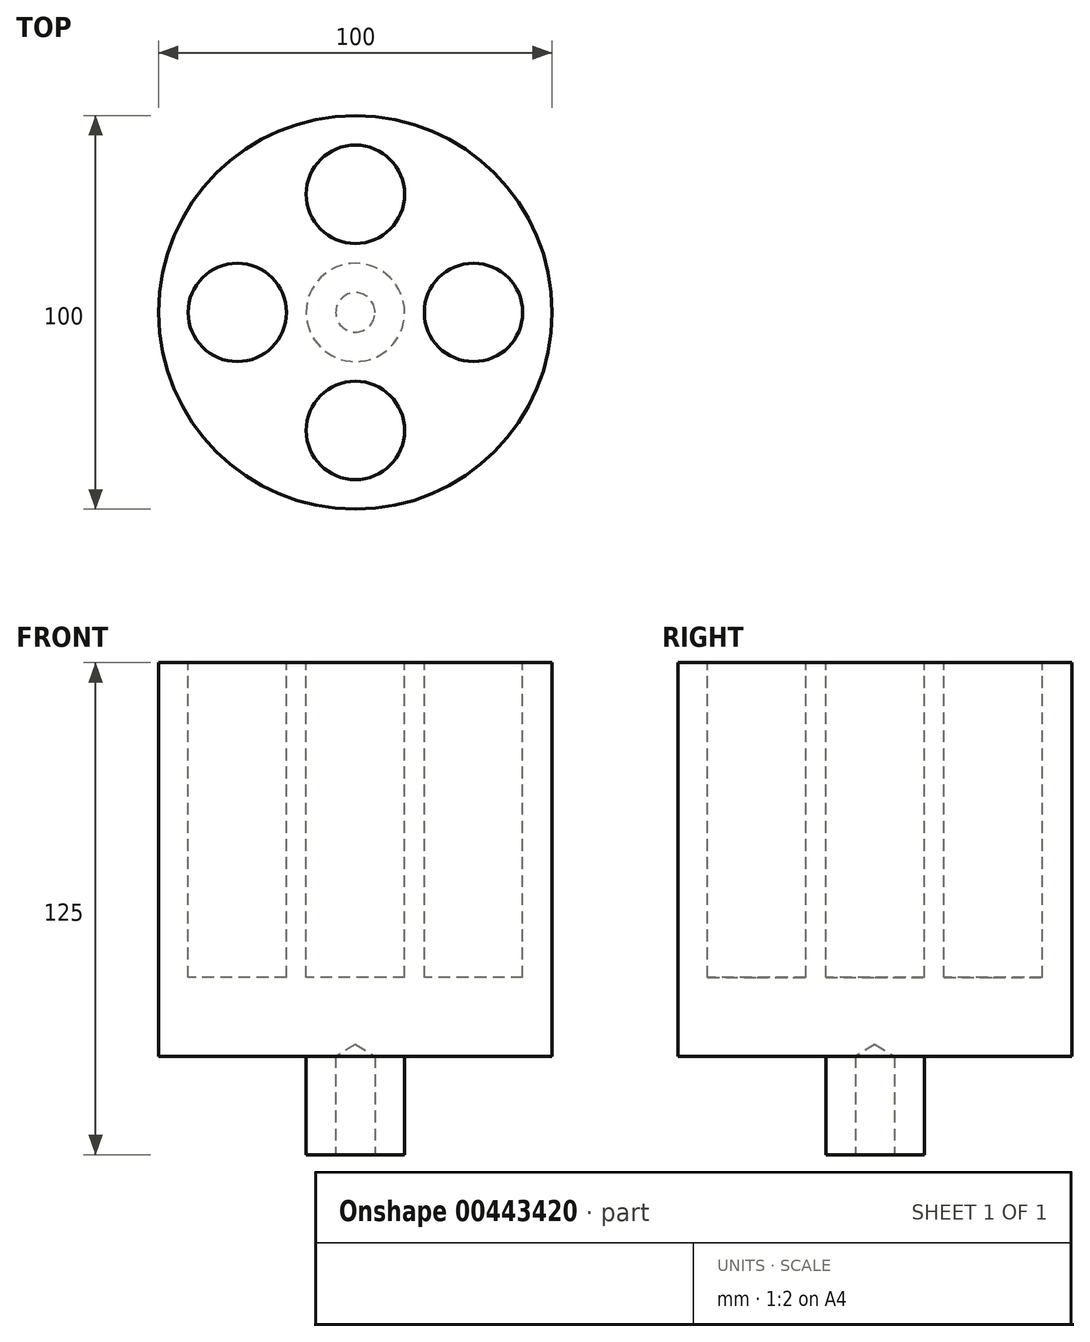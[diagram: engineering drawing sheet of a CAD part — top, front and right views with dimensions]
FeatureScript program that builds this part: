
annotation { "Feature Type Name" : "Feature", "Feature Type Description" : "" }
export const myFeature = defineFeature(function(context is Context, id is Id, definition is map)
    precondition{}
    {
        {
            var Q0;
            Q0=qCreatedBy(makeId("Top.planeOp"),FACE);
            var sketch = newSketch(context, id + "F0", { "sketchPlane" : qUnion([Q0])});
            skCircle(sketch, "E0", {"center": v(0, 0) * mm, "radius": 50 * mm});
            skSolve(sketch);
        }
        {
            var Q0;
            Q0=makeQuery(id+"F0.imprint","IMPRINT",FACE,{"disambiguationData":[TD([[makeQuery(id+"F0.imprint","IMPRINT",EDGE,{"derivedFrom":sQuery(id+"F0.wireOp",EDGE,"E0")}),1.0]])]});
            extrude(context, id + "F1", {"entities" : qUnion([Q0]), "depth" : 100 * mm});
        }
        {
            var Q0;
            Q0=makeQuery(id+"F1.opExtrude","CAP_FACE",FACE,{"disambiguationData":[OSD([sQuery(id+"F0.wireOp",EDGE,"E0")])],"isStart":true});
            var sketch = newSketch(context, id + "F2", { "sketchPlane" : qUnion([Q0])});
            skCircle(sketch, "E1", {"center": v(0, 0) * mm, "radius": 12.5 * mm});
            skSolve(sketch);
        }
        {
            var Q0;
            Q0=makeQuery(id+"F2.imprint","IMPRINT",FACE,{"disambiguationData":[TD([[makeQuery(id+"F2.imprint","IMPRINT",EDGE,{"derivedFrom":sQuery(id+"F2.wireOp",EDGE,"E1")}),1.0]])]});
            extrude(context, id + "F3", {"entities" : qUnion([Q0]), "operationType" : NewBodyOperationType.ADD, "depth" : 25 * mm});
        }
        {
            var Q0;
            Q0=makeQuery(id+"F3.opExtrude","CAP_FACE",FACE,{"disambiguationData":[OSD([sQuery(id+"F2.wireOp",EDGE,"E1")])],"isStart":false});
            var sketch = newSketch(context, id + "F4", { "sketchPlane" : qUnion([Q0])});
            skPoint(sketch, "E2", {"position": v(0, 0) * mm});
            skSolve(sketch);
        }
        {
            var Q0;
            Q0=sQuery(id+"F4.wireOp",VERTEX,"E2");
            var Q1;
            Q1=makeQuery(id+"F1.opExtrude","SWEPT_BODY",BODY,{"disambiguationData":[OSD([sQuery(id+"F0.wireOp",EDGE,"E0")])]});
            hole(context, id + "F5", {"style" : HoleStyle.SIMPLE, "endStyle" : HoleEndStyle.BLIND, "holeDiameter" : 10 * mm, "holeDepth" : 25 * mm, "isTappedThrough" : true, "tappedDepth" : 12 * mm, "tapClearance" : 3, "startFromSketch" : true, "locations" : qUnion([Q0]), "scope" : qUnion([Q1])});
        }
        {
            var Q0;
            Q0=makeQuery(id+"F1.opExtrude","CAP_FACE",FACE,{"disambiguationData":[OSD([sQuery(id+"F0.wireOp",EDGE,"E0")])],"isStart":false});
            var sketch = newSketch(context, id + "F6", { "sketchPlane" : qUnion([Q0])});
            skCircle(sketch, "E3", {"center": v(0, 0) * mm, "radius": 30 * mm, "construction": true});
            skCircle(sketch, "E4", {"center": v(-30, 0) * mm, "radius": 12.5 * mm});
            skCircle(sketch, "E5.1.0", {"center": v(0, -30) * mm, "radius": 12.5 * mm});
            skCircle(sketch, "E5.2.0", {"center": v(30, 0) * mm, "radius": 12.5 * mm});
            skCircle(sketch, "E5.3.0", {"center": v(0, 30) * mm, "radius": 12.5 * mm});
            skSolve(sketch);
        }
        {
            var Q0;
            Q0=makeQuery(id+"F6.imprint","IMPRINT",FACE,{"disambiguationData":[TD([[makeQuery(id+"F6.imprint","IMPRINT",EDGE,{"derivedFrom":sQuery(id+"F6.wireOp",EDGE,"E4")}),1.0]])]});
            var Q1;
            Q1=makeQuery(id+"F6.imprint","IMPRINT",FACE,{"disambiguationData":[TD([[makeQuery(id+"F6.imprint","IMPRINT",EDGE,{"derivedFrom":sQuery(id+"F6.wireOp",EDGE,"E5.1.0")}),1.0]])]});
            var Q2;
            Q2=makeQuery(id+"F6.imprint","IMPRINT",FACE,{"disambiguationData":[TD([[makeQuery(id+"F6.imprint","IMPRINT",EDGE,{"derivedFrom":sQuery(id+"F6.wireOp",EDGE,"E5.2.0")}),1.0]])]});
            var Q3;
            Q3=makeQuery(id+"F6.imprint","IMPRINT",FACE,{"disambiguationData":[TD([[makeQuery(id+"F6.imprint","IMPRINT",EDGE,{"derivedFrom":sQuery(id+"F6.wireOp",EDGE,"E5.3.0")}),1.0]])]});
            extrude(context, id + "F7", {"entities" : qUnion([Q0, Q1, Q2, Q3]), "operationType" : NewBodyOperationType.REMOVE, "oppositeDirection" : true, "depth" : 80 * mm});
        }
    });
